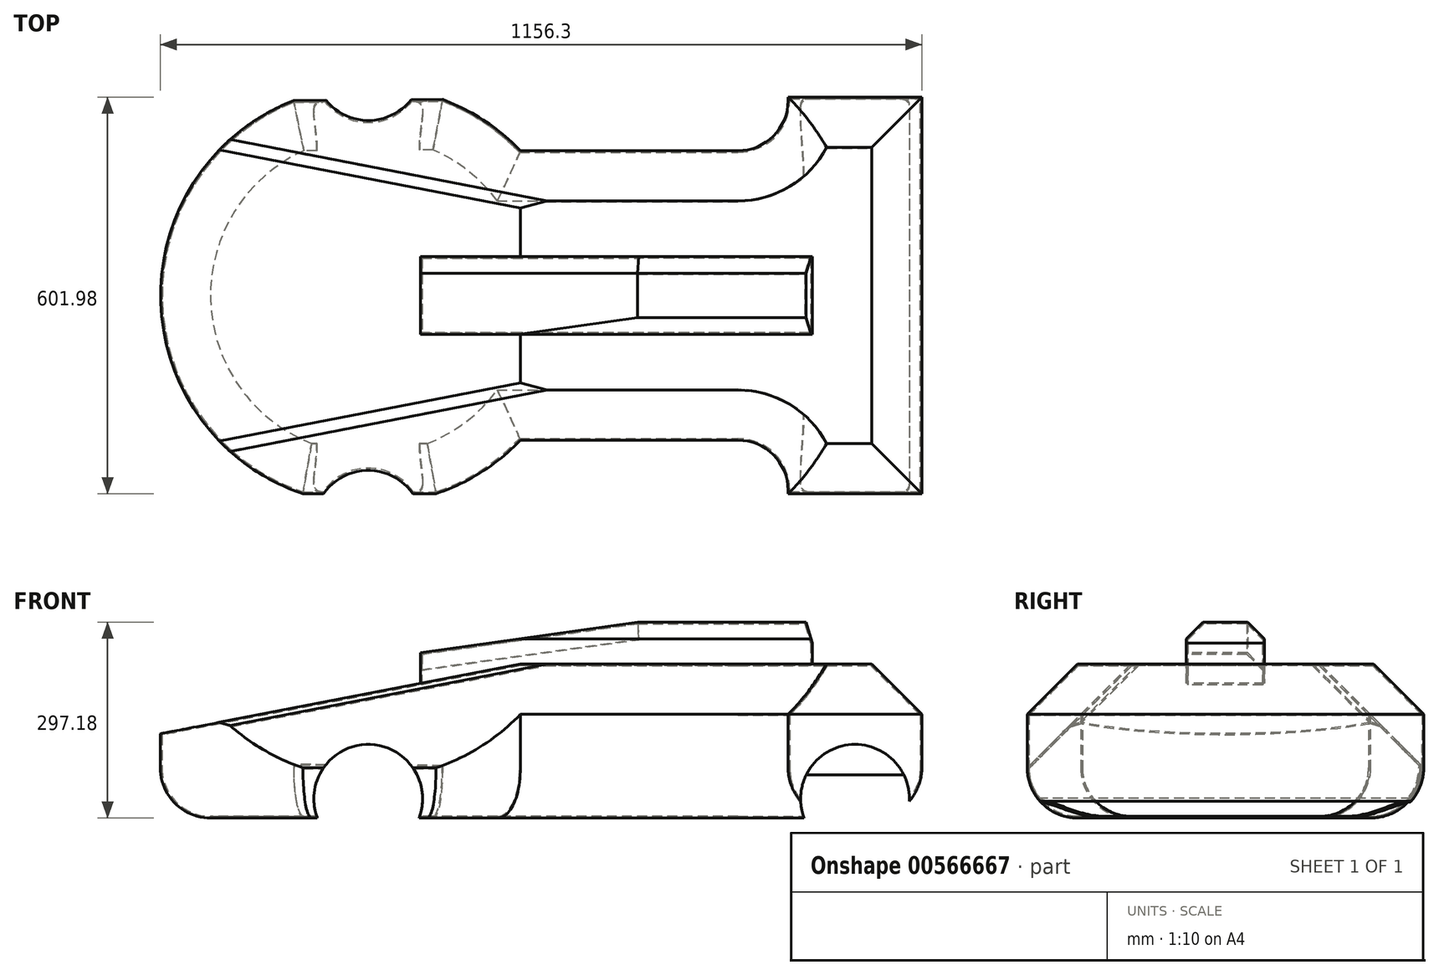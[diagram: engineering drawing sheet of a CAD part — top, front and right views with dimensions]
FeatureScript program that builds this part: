
annotation { "Feature Type Name" : "Feature", "Feature Type Description" : "" }
export const myFeature = defineFeature(function(context is Context, id is Id, definition is map)
    precondition{}
    {
        {
            var Q0;
            Q0=qCreatedBy(makeId("Top.planeOp"),FACE);
            var sketch = newSketch(context, id + "F0", { "sketchPlane" : qUnion([Q0])});
            skArc(sketch, "E0", {"start": v(-552.25, 219.71) * mm, "mid": v(-607.01, 265.29) * mm, "end": v(-670.56, 297.5) * mm});
            skLineSegment(sketch, "E1.bottom", {"start": v(-552.25, 219.7) * mm, "end": v(-222.05, 219.7) * mm});
            skLineSegment(sketch, "E1.top", {"start": v(-552.25, -219.7) * mm, "end": v(-222.05, -219.7) * mm});
            skLineSegment(sketch, "E2.bottom", {"start": v(-145.85, 301) * mm, "end": v(57.35, 301) * mm});
            skLineSegment(sketch, "E2.top", {"start": v(-145.85, -301) * mm, "end": v(57.35, -301) * mm});
            skLineSegment(sketch, "E2.left", {"start": v(-145.85, 300.99) * mm, "end": v(-145.85, 295.91) * mm});
            skLineSegment(sketch, "E2.right", {"start": v(57.35, 300.99) * mm, "end": v(57.35, -300.99) * mm});
            skPoint(sketch, "E3.orphan", {"position": v(-781.45, 219.7) * mm});
            skPoint(sketch, "E4.orphan", {"position": v(-781.45, -219.7) * mm});
            skLineSegment(sketch, "E5.trimOffspring", {"start": v(-145.85, -295.91) * mm, "end": v(-145.85, -300.99) * mm});
            skPoint(sketch, "E6.orphan", {"position": v(0, 219.7) * mm});
            skPoint(sketch, "E7.orphan", {"position": v(0, -219.7) * mm});
            skPoint(sketch, "E8.visualSharp", {"position": v(-145.85, 219.7) * mm});
            skArc(sketch, "E8.filletArc", {"start": v(-222.05, 219.71) * mm, "mid": v(-168.17, 242.03) * mm, "end": v(-145.85, 295.91) * mm});
            skPoint(sketch, "E9.visualSharp", {"position": v(-145.85, -219.7) * mm});
            skArc(sketch, "E9.filletArc", {"start": v(-145.85, -295.91) * mm, "mid": v(-168.17, -242.03) * mm, "end": v(-222.05, -219.71) * mm});
            skLineSegment(sketch, "E10", {"start": v(-145.85, 301.2) * mm, "end": v(-176.43, 300.99) * mm});
            skLineSegment(sketch, "E11", {"start": v(-145.85, -301) * mm, "end": v(-167.87, -301) * mm});
            skArc(sketch, "E12.trimOffspring", {"start": v(-896.53, 295.91) * mm, "mid": v(-1098.86, -7.46) * mm, "end": v(-882.5, -301) * mm});
            skArc(sketch, "E13.trimOffspring", {"start": v(-680.4, -301) * mm, "mid": v(-611.4, -268.12) * mm, "end": v(-552.25, -219.71) * mm});
            skLineSegment(sketch, "E14.trimOffspring", {"start": v(-680.4, -301) * mm, "end": v(-882.5, -301) * mm});
            skLineSegment(sketch, "E15.trimOffspring", {"start": v(-670.56, 297.5) * mm, "end": v(-896.53, 295.91) * mm});
            skSolve(sketch);
        }
        {
            var Q0;
            Q0 = qSketchRegion(id + "F0", true);
            extrude(context, id + "F1", {"entities" : qUnion([Q0]), "depth" : 233.68 * mm, "offsetDistance" : 25.4 * mm});
        }
        {
            var Q0;
            Q0=makeQuery(id+"F1.opExtrude","SWEPT_FACE",FACE,{"disambiguationData":[OSD([sQuery(id+"F0.wireOp",EDGE,"E1.top")])]});
            var sketch = newSketch(context, id + "F2", { "sketchPlane" : qUnion([Q0])});
            skLineSegment(sketch, "E16", {"start": v(-552.25, 233.68) * mm, "end": v(-1099.56, 127.83) * mm});
            skLineSegment(sketch, "E17", {"start": v(-1099.56, 127.83) * mm, "end": v(-1099.56, 233.68) * mm});
            skLineSegment(sketch, "E18", {"start": v(-1099.56, 233.68) * mm, "end": v(-552.25, 233.68) * mm});
            skSolve(sketch);
        }
        {
            var Q0;
            Q0 = qSketchRegion(id + "F2", true);
            extrude(context, id + "F3", {"entities" : qUnion([Q0]), "operationType" : NewBodyOperationType.REMOVE, "oppositeDirection" : true, "depth" : 439.42 * mm, "offsetDistance" : 25.4 * mm});
        }
        {
            var Q0;
            Q0=makeQuery(id+"F1.opExtrude","CAP_FACE",FACE,{"disambiguationData":[OSD([sQuery(id+"F0.wireOp",EDGE,"E0"),sQuery(id+"F0.wireOp",EDGE,"E1.bottom"),sQuery(id+"F0.wireOp",EDGE,"E1.top"),sQuery(id+"F0.wireOp",EDGE,"E2.bottom"),sQuery(id+"F0.wireOp",EDGE,"E2.top"),sQuery(id+"F0.wireOp",EDGE,"E2.left"),sQuery(id+"F0.wireOp",EDGE,"E2.right"),sQuery(id+"F0.wireOp",EDGE,"E5.trimOffspring"),sQuery(id+"F0.wireOp",EDGE,"E8.filletArc"),sQuery(id+"F0.wireOp",EDGE,"E9.filletArc"),sQuery(id+"F0.wireOp",EDGE,"E12.trimOffspring"),sQuery(id+"F0.wireOp",EDGE,"E13.trimOffspring"),sQuery(id+"F0.wireOp",EDGE,"E14.trimOffspring"),sQuery(id+"F0.wireOp",EDGE,"E15.trimOffspring")])],"isStart":true});
            fillet(context, id + "F4", {"entities" : qUnion([Q0]), "radius" : 76.2 * mm, "tangentPropagation" : true, "allowEdgeOverflow" : false});
        }
        {
            var Q0;
            Q0=makeQuery(id+"F3.boolean.opBoolean","COPY",FACE,{"derivedFrom":makeQuery(id+"F3.opExtrude","CAP_FACE",FACE,{"disambiguationData":[OSD([sQuery(id+"F2.wireOp",EDGE,"E16"),sQuery(id+"F2.wireOp",EDGE,"E17"),sQuery(id+"F2.wireOp",EDGE,"E18")])],"isStart":false})});
            var sketch = newSketch(context, id + "F5", { "sketchPlane" : qUnion([Q0])});
            skLineSegment(sketch, "E19", {"start": v(-552.25, 233.68) * mm, "end": v(-1010.65, 145.02) * mm});
            skLineSegment(sketch, "E20", {"start": v(-1010.65, 145.02) * mm, "end": v(-1010.65, 233.68) * mm});
            skLineSegment(sketch, "E21", {"start": v(-1010.65, 233.68) * mm, "end": v(-552.25, 233.68) * mm});
            skSolve(sketch);
        }
        {
            var Q0;
            Q0 = qSketchRegion(id + "F5", true);
            extrude(context, id + "F6", {"entities" : qUnion([Q0]), "operationType" : NewBodyOperationType.REMOVE, "oppositeDirection" : true, "depth" : 81.28 * mm, "offsetDistance" : 25.4 * mm});
        }
        {
            var Q0;
            Q0=makeQuery(id+"F3.boolean.opBoolean","COPY",FACE,{"derivedFrom":makeQuery(id+"F3.opExtrude","CAP_FACE",FACE,{"disambiguationData":[OSD([sQuery(id+"F2.wireOp",EDGE,"E16"),sQuery(id+"F2.wireOp",EDGE,"E17"),sQuery(id+"F2.wireOp",EDGE,"E18")])],"isStart":true})});
            var sketch = newSketch(context, id + "F7", { "sketchPlane" : qUnion([Q0])});
            skLineSegment(sketch, "E22", {"start": v(552.25, 233.68) * mm, "end": v(1010.65, 233.68) * mm});
            skLineSegment(sketch, "E23", {"start": v(1010.65, 233.68) * mm, "end": v(1010.65, 145.02) * mm});
            skLineSegment(sketch, "E24", {"start": v(1010.65, 145.02) * mm, "end": v(552.25, 233.68) * mm});
            skSolve(sketch);
        }
        {
            var Q0;
            Q0 = qSketchRegion(id + "F7", true);
            extrude(context, id + "F8", {"entities" : qUnion([Q0]), "operationType" : NewBodyOperationType.REMOVE, "oppositeDirection" : true, "depth" : 83.82 * mm, "offsetDistance" : 25.4 * mm});
        }
        {
            var Q0;
            Q0=makeQuery(id+"F1.opExtrude","CAP_EDGE",EDGE,{"disambiguationData":[OSD([sQuery(id+"F0.wireOp",EDGE,"E2.top")])],"isStart":false});
            var Q1;
            Q1=makeQuery(id+"F1.opExtrude","CAP_EDGE",EDGE,{"disambiguationData":[OSD([sQuery(id+"F0.wireOp",EDGE,"E2.right")])],"isStart":false});
            var Q2;
            Q2=makeQuery(id+"F1.opExtrude","CAP_EDGE",EDGE,{"disambiguationData":[OSD([sQuery(id+"F0.wireOp",EDGE,"E2.bottom")])],"isStart":false});
            chamfer(context, id + "F9", {"entities" : qUnion([Q0, Q1, Q2]), "width" : 76.2 * mm, "tangentPropagation" : true});
        }
        {
            var Q0;
            Q0=makeQuery(id+"F1.opExtrude","CAP_EDGE",EDGE,{"disambiguationData":[OSD([sQuery(id+"F0.wireOp",EDGE,"E1.top")])],"isStart":false});
            var Q1;
            Q1=makeQuery(id+"F1.opExtrude","CAP_EDGE",EDGE,{"disambiguationData":[OSD([sQuery(id+"F0.wireOp",EDGE,"E1.bottom")])],"isStart":false});
            chamfer(context, id + "F10", {"entities" : qUnion([Q0, Q1]), "width" : 76.2 * mm, "tangentPropagation" : true});
        }
        {
            var Q0;
            Q0=makeQuery(id+"F10.opChamfer","BLEND_EDGE",EDGE,{"blendedFrom":[makeQuery(id+"F1.opExtrude","CAP_EDGE",EDGE,{"disambiguationData":[OSD([sQuery(id+"F0.wireOp",EDGE,"E1.top")])],"isStart":false}),makeQuery(id+"F8.boolean.opBoolean","MERGE",FACE,{"derivedFrom":[makeQuery(id+"F6.boolean.opBoolean","MERGE",FACE,{"derivedFrom":[makeQuery(id+"F3.boolean.opBoolean","COPY",FACE,{"derivedFrom":makeQuery(id+"F3.opExtrude","SWEPT_FACE",FACE,{"disambiguationData":[OSD([sQuery(id+"F2.wireOp",EDGE,"E16")])]})}),makeQuery(id+"F6.opExtrude","SWEPT_FACE",FACE,{"disambiguationData":[OSD([sQuery(id+"F5.wireOp",EDGE,"E19")])]})]}),makeQuery(id+"F8.opExtrude","SWEPT_FACE",FACE,{"disambiguationData":[OSD([sQuery(id+"F7.wireOp",EDGE,"E24")])]})]})],"blendedInto":[makeQuery(id+"F8.boolean.opBoolean","MERGE",FACE,{"derivedFrom":[makeQuery(id+"F6.boolean.opBoolean","MERGE",FACE,{"derivedFrom":[makeQuery(id+"F3.boolean.opBoolean","COPY",FACE,{"derivedFrom":makeQuery(id+"F3.opExtrude","SWEPT_FACE",FACE,{"disambiguationData":[OSD([sQuery(id+"F2.wireOp",EDGE,"E16")])]})}),makeQuery(id+"F6.opExtrude","SWEPT_FACE",FACE,{"disambiguationData":[OSD([sQuery(id+"F5.wireOp",EDGE,"E19")])]})]}),makeQuery(id+"F8.opExtrude","SWEPT_FACE",FACE,{"disambiguationData":[OSD([sQuery(id+"F7.wireOp",EDGE,"E24")])]})]})]});
            var Q1;
            Q1=makeQuery(id+"F10.opChamfer","BLEND_EDGE",EDGE,{"blendedFrom":[makeQuery(id+"F1.opExtrude","CAP_EDGE",EDGE,{"disambiguationData":[OSD([sQuery(id+"F0.wireOp",EDGE,"E1.bottom")])],"isStart":false}),makeQuery(id+"F8.boolean.opBoolean","MERGE",FACE,{"derivedFrom":[makeQuery(id+"F6.boolean.opBoolean","MERGE",FACE,{"derivedFrom":[makeQuery(id+"F3.boolean.opBoolean","COPY",FACE,{"derivedFrom":makeQuery(id+"F3.opExtrude","SWEPT_FACE",FACE,{"disambiguationData":[OSD([sQuery(id+"F2.wireOp",EDGE,"E16")])]})}),makeQuery(id+"F6.opExtrude","SWEPT_FACE",FACE,{"disambiguationData":[OSD([sQuery(id+"F5.wireOp",EDGE,"E19")])]})]}),makeQuery(id+"F8.opExtrude","SWEPT_FACE",FACE,{"disambiguationData":[OSD([sQuery(id+"F7.wireOp",EDGE,"E24")])]})]})],"blendedInto":[makeQuery(id+"F8.boolean.opBoolean","MERGE",FACE,{"derivedFrom":[makeQuery(id+"F6.boolean.opBoolean","MERGE",FACE,{"derivedFrom":[makeQuery(id+"F3.boolean.opBoolean","COPY",FACE,{"derivedFrom":makeQuery(id+"F3.opExtrude","SWEPT_FACE",FACE,{"disambiguationData":[OSD([sQuery(id+"F2.wireOp",EDGE,"E16")])]})}),makeQuery(id+"F6.opExtrude","SWEPT_FACE",FACE,{"disambiguationData":[OSD([sQuery(id+"F5.wireOp",EDGE,"E19")])]})]}),makeQuery(id+"F8.opExtrude","SWEPT_FACE",FACE,{"disambiguationData":[OSD([sQuery(id+"F7.wireOp",EDGE,"E24")])]})]})]});
            chamfer(context, id + "F11", {"entities" : qUnion([Q0, Q1]), "width" : 25.4 * mm, "tangentPropagation" : true});
        }
        {
            var Q0;
            {var subQ0=sQuery(id+"F0.wireOp",EDGE,"E8.filletArc");var subQ1=sQuery(id+"F0.wireOp",EDGE,"E5.trimOffspring");var subQ2=sQuery(id+"F0.wireOp",EDGE,"E2.right");var subQ3=sQuery(id+"F0.wireOp",EDGE,"E2.left");var subQ4=sQuery(id+"F0.wireOp",EDGE,"E2.top");var subQ8=sQuery(id+"F0.wireOp",EDGE,"E2.bottom");var subQ9=sQuery(id+"F0.wireOp",EDGE,"E0");var subQ10=sQuery(id+"F0.wireOp",EDGE,"E13.trimOffspring");var subQ11=sQuery(id+"F0.wireOp",EDGE,"E9.filletArc");var subQ12=sQuery(id+"F0.wireOp",EDGE,"E1.top");var subQ13=sQuery(id+"F0.wireOp",EDGE,"E1.bottom");var subQ14=makeQuery(id+"F1.opExtrude","CAP_FACE",FACE,{"disambiguationData":[OSD([subQ9,subQ13,subQ12,subQ8,subQ4,subQ3,subQ2,subQ1,subQ0,subQ11,sQuery(id+"F0.wireOp",EDGE,"E12.trimOffspring"),subQ10,sQuery(id+"F0.wireOp",EDGE,"E14.trimOffspring"),sQuery(id+"F0.wireOp",EDGE,"E15.trimOffspring")])],"isStart":false});Q0=makeQuery(id+"F3.boolean.opBoolean","SPLIT",FACE,{"disambiguationData":[TD([makeQuery(id+"F1.opExtrude","SWEPT_FACE",FACE,{"disambiguationData":[OSD([subQ8])]})])],"derivedFrom":subQ14});}
            var sketch = newSketch(context, id + "F12", { "sketchPlane" : qUnion([Q0])});
            skPoint(sketch, "E25.firstSnap0", {"position": v(-18.85, 58.83) * mm});
            skPoint(sketch, "E25.oppositeSnap0", {"position": v(-704.13, -117.66) * mm});
            skPoint(sketch, "E25.oppositeSnap1", {"position": v(-552.25, -59.37) * mm});
            skLineSegment(sketch, "E25.bottom", {"start": v(-109.19, 58.83) * mm, "end": v(-704.13, 58.83) * mm});
            skLineSegment(sketch, "E25.top", {"start": v(-109.19, -59.37) * mm, "end": v(-704.13, -59.37) * mm});
            skLineSegment(sketch, "E25.left", {"start": v(-109.19, 58.83) * mm, "end": v(-109.19, -59.37) * mm});
            skLineSegment(sketch, "E25.right", {"start": v(-704.13, 58.83) * mm, "end": v(-704.13, -59.37) * mm});
            skSolve(sketch);
        }
        {
            var Q0;
            Q0 = qSketchRegion(id + "F12", true);
            extrude(context, id + "F13", {"entities" : qUnion([Q0]), "operationType" : NewBodyOperationType.ADD, "endBound" : BoundingType.UP_TO_NEXT, "oppositeDirection" : true, "depth" : 30.48 * mm, "offsetDistance" : 25.4 * mm});
        }
        {
            var Q0;
            Q0 = qSketchRegion(id + "F12", true);
            extrude(context, id + "F14", {"entities" : qUnion([Q0]), "operationType" : NewBodyOperationType.ADD, "depth" : 63.5 * mm, "offsetDistance" : 25.4 * mm});
        }
        {
            var Q0;
            {var subQ0=sQuery(id+"F12.wireOp",EDGE,"E25.top");Q0=makeQuery(id+"F14.boolean.opBoolean","MERGE",FACE,{"derivedFrom":[makeQuery(id+"F13.opExtrude","SWEPT_FACE",FACE,{"disambiguationData":[OSD([subQ0])]}),makeQuery(id+"F14.opExtrude","SWEPT_FACE",FACE,{"disambiguationData":[OSD([subQ0])]})]});}
            var sketch = newSketch(context, id + "F15", { "sketchPlane" : qUnion([Q0])});
            skLineSegment(sketch, "E26", {"start": v(-704.13, 250.74) * mm, "end": v(-374.16, 297.18) * mm});
            skLineSegment(sketch, "E27", {"start": v(-374.16, 297.18) * mm, "end": v(-704.13, 297.18) * mm});
            skLineSegment(sketch, "E28", {"start": v(-704.13, 297.18) * mm, "end": v(-704.13, 250.74) * mm});
            skSolve(sketch);
        }
        {
            var Q0;
            Q0 = qSketchRegion(id + "F15", true);
            extrude(context, id + "F16", {"entities" : qUnion([Q0]), "operationType" : NewBodyOperationType.REMOVE, "oppositeDirection" : true, "depth" : 122.94 * mm, "offsetDistance" : 25.4 * mm});
        }
        {
            var Q0;
            {var subQ0=sQuery(id+"F12.wireOp",EDGE,"E25.top");Q0=makeQuery(id+"F14.boolean.opBoolean","MERGE",FACE,{"derivedFrom":[makeQuery(id+"F13.opExtrude","SWEPT_FACE",FACE,{"disambiguationData":[OSD([subQ0])]}),makeQuery(id+"F14.opExtrude","SWEPT_FACE",FACE,{"disambiguationData":[OSD([subQ0])]})]});}
            var sketch = newSketch(context, id + "F17", { "sketchPlane" : qUnion([Q0])});
            skLineSegment(sketch, "E29", {"start": v(-109.19, 265.43) * mm, "end": v(-118.25, 297.18) * mm});
            skLineSegment(sketch, "E30", {"start": v(-118.25, 297.18) * mm, "end": v(-109.19, 297.18) * mm});
            skLineSegment(sketch, "E31", {"start": v(-109.19, 297.18) * mm, "end": v(-109.19, 265.43) * mm});
            skSolve(sketch);
        }
        {
            var Q0;
            Q0 = qSketchRegion(id + "F17", true);
            extrude(context, id + "F18", {"entities" : qUnion([Q0]), "operationType" : NewBodyOperationType.REMOVE, "oppositeDirection" : true, "depth" : 120.14 * mm, "offsetDistance" : 25.4 * mm});
        }
        {
            var Q0;
            Q0=makeQuery(id+"F16.boolean.opBoolean","COPY",EDGE,{"derivedFrom":makeQuery(id+"F16.opExtrude","CAP_EDGE",EDGE,{"disambiguationData":[OSD([sQuery(id+"F15.wireOp",EDGE,"E26")])],"isStart":true})});
            var Q1;
            Q1=makeQuery(id+"F14.opExtrude","CAP_EDGE",EDGE,{"disambiguationData":[OSD([sQuery(id+"F12.wireOp",EDGE,"E25.top")])],"isStart":false});
            var Q2;
            Q2=makeQuery(id+"F18.boolean.opBoolean","COPY",EDGE,{"derivedFrom":makeQuery(id+"F18.opExtrude","SWEPT_EDGE",EDGE,{"disambiguationData":[OSD([sQuery(id+"F12.wireOp",EDGE,"E25.top"),sQuery(id+"F17.wireOp",EDGE,"E29"),sQuery(id+"F17.wireOp",EDGE,"E30")])]})});
            var Q3;
            Q3=makeQuery(id+"F14.opExtrude","CAP_EDGE",EDGE,{"disambiguationData":[OSD([sQuery(id+"F12.wireOp",EDGE,"E25.bottom")])],"isStart":false});
            var Q4;
            {var subQ0=sQuery(id+"F12.wireOp",EDGE,"E25.bottom");Q4=makeQuery(id+"F16.boolean.opBoolean","INTERSECT",EDGE,{"derivedFrom":[makeQuery(id+"F14.boolean.opBoolean","MERGE",FACE,{"derivedFrom":[makeQuery(id+"F13.opExtrude","SWEPT_FACE",FACE,{"disambiguationData":[OSD([subQ0])]}),makeQuery(id+"F14.opExtrude","SWEPT_FACE",FACE,{"disambiguationData":[OSD([subQ0])]})]}),makeQuery(id+"F16.opExtrude","SWEPT_FACE",FACE,{"disambiguationData":[OSD([sQuery(id+"F15.wireOp",EDGE,"E26")])]})]});}
            var Q5;
            Q5=makeQuery(id+"F16.boolean.opBoolean","COPY",EDGE,{"derivedFrom":makeQuery(id+"F16.opExtrude","SWEPT_EDGE",EDGE,{"disambiguationData":[OSD([sQuery(id+"F12.wireOp",EDGE,"E25.top"),sQuery(id+"F12.wireOp",EDGE,"E25.right"),sQuery(id+"F15.wireOp",EDGE,"E26"),sQuery(id+"F15.wireOp",EDGE,"E28")])]})});
            chamfer(context, id + "F19", {"entities" : qUnion([Q0, Q1, Q2, Q3, Q4, Q5]), "width" : 25.4 * mm, "tangentPropagation" : true});
        }
        {
            var Q0;
            Q0=makeQuery(id+"F1.opExtrude","CAP_FACE",FACE,{"disambiguationData":[OSD([sQuery(id+"F0.wireOp",EDGE,"E0"),sQuery(id+"F0.wireOp",EDGE,"E1.bottom"),sQuery(id+"F0.wireOp",EDGE,"E1.top"),sQuery(id+"F0.wireOp",EDGE,"E2.bottom"),sQuery(id+"F0.wireOp",EDGE,"E2.top"),sQuery(id+"F0.wireOp",EDGE,"E2.left"),sQuery(id+"F0.wireOp",EDGE,"E2.right"),sQuery(id+"F0.wireOp",EDGE,"E5.trimOffspring"),sQuery(id+"F0.wireOp",EDGE,"E8.filletArc"),sQuery(id+"F0.wireOp",EDGE,"E9.filletArc"),sQuery(id+"F0.wireOp",EDGE,"E12.trimOffspring"),sQuery(id+"F0.wireOp",EDGE,"E13.trimOffspring"),sQuery(id+"F0.wireOp",EDGE,"E14.trimOffspring"),sQuery(id+"F0.wireOp",EDGE,"E15.trimOffspring")])],"isStart":true});
            shell(context, id + "F20", {"entities" : qUnion([Q0]), "thickness" : 2.54 * mm});
        }
        {
            var Q0;
            Q0=makeQuery(id+"F1.opExtrude","SWEPT_FACE",FACE,{"disambiguationData":[OSD([sQuery(id+"F0.wireOp",EDGE,"E2.top")])]});
            var sketch = newSketch(context, id + "F21", { "sketchPlane" : qUnion([Q0])});
            skCircle(sketch, "E32", {"center": v(-44.25, 29.2) * mm, "radius": 82.55 * mm});
            skPoint(sketch, "E32.centerSnap0", {"position": v(-44.25, 76.2) * mm});
            skCircle(sketch, "E33", {"center": v(-783.32, 29.2) * mm, "radius": 82.55 * mm});
            skSolve(sketch);
        }
        {
            var Q0;
            Q0 = qSketchRegion(id + "F21", true);
            extrude(context, id + "F22", {"entities" : qUnion([Q0]), "operationType" : NewBodyOperationType.REMOVE, "oppositeDirection" : true, "depth" : 601.22 * mm, "offsetDistance" : 25.4 * mm});
        }
    });
